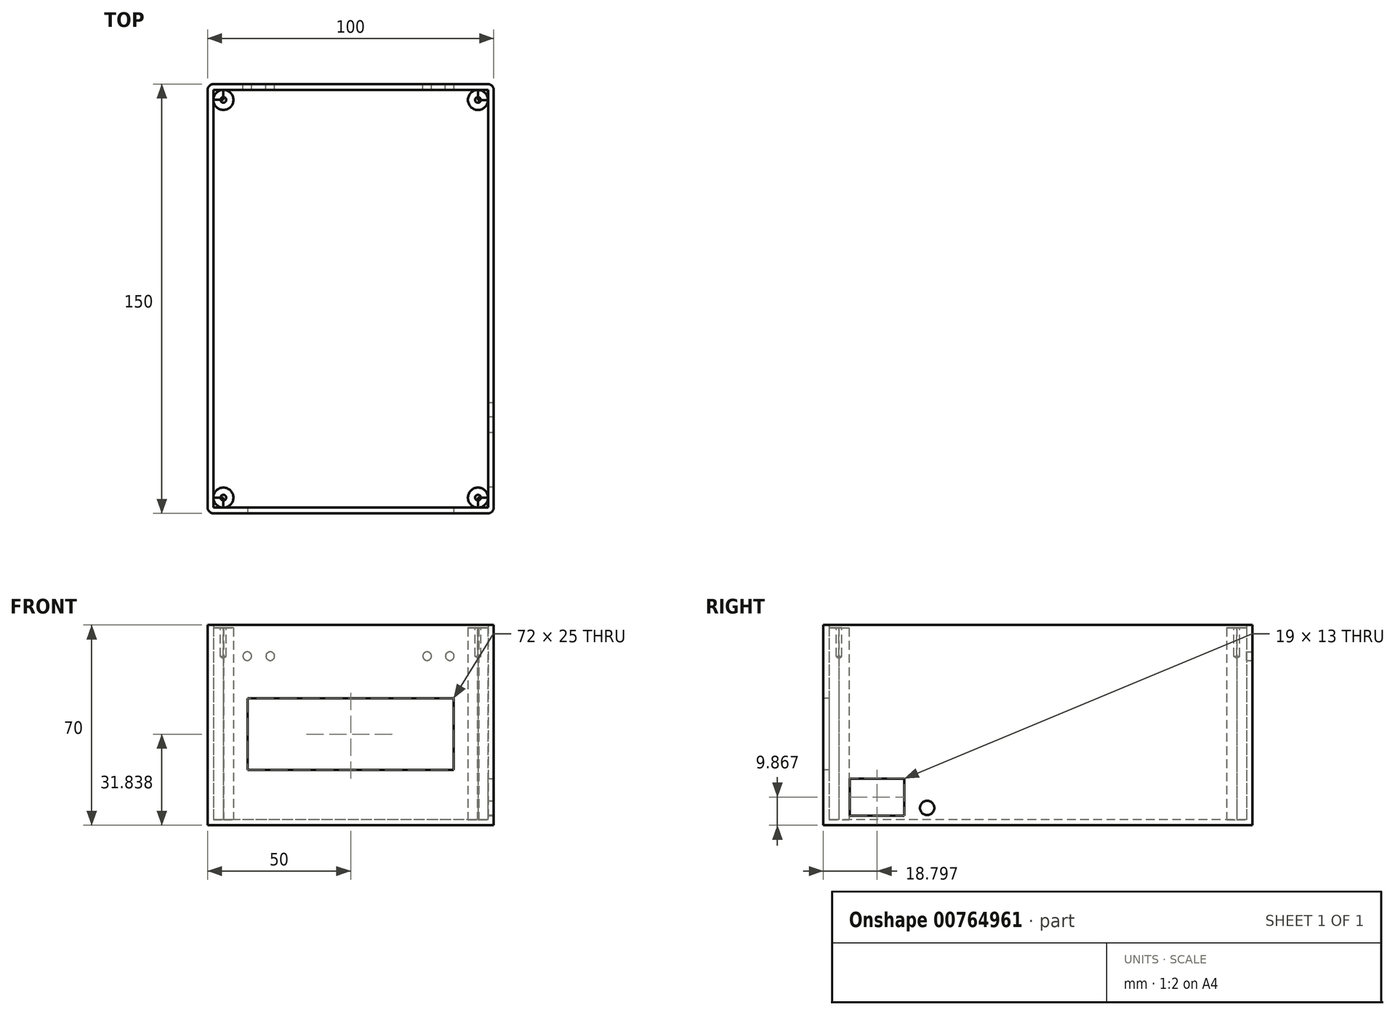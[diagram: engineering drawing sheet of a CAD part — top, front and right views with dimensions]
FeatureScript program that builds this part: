
annotation { "Feature Type Name" : "Feature", "Feature Type Description" : "" }
export const myFeature = defineFeature(function(context is Context, id is Id, definition is map)
    precondition{}
    {
        {
            var Q0;
            Q0=qCreatedBy(makeId("Top.planeOp"),FACE);
            var sketch = newSketch(context, id + "F0", { "sketchPlane" : qUnion([Q0])});
            skLineSegment(sketch, "E0.bottom", {"start": v(50, 75) * mm, "end": v(-50, 75) * mm});
            skLineSegment(sketch, "E0.top", {"start": v(50, -75) * mm, "end": v(-50, -75) * mm});
            skLineSegment(sketch, "E0.left", {"start": v(50, 75) * mm, "end": v(50, -75) * mm});
            skLineSegment(sketch, "E0.right", {"start": v(-50, 75) * mm, "end": v(-50, -75) * mm});
            skPoint(sketch, "E0.middle", {"position": v(0, 0) * mm});
            skSolve(sketch);
        }
        {
            var Q0;
            Q0=qSketchRegion(id+"F0",true);
            extrude(context, id + "F1", {"entities" : qUnion([Q0]), "depth" : 70 * mm, "offsetDistance" : 25.4 * mm});
        }
        {
            var Q0;
            Q0=makeQuery(id+"F1.opExtrude","CAP_FACE",FACE,{"disambiguationData":[OSD([sQuery(id+"F0.wireOp",EDGE,"E0.bottom"),sQuery(id+"F0.wireOp",EDGE,"E0.top"),sQuery(id+"F0.wireOp",EDGE,"E0.left"),sQuery(id+"F0.wireOp",EDGE,"E0.right")])],"isStart":false});
            shell(context, id + "F2", {"entities" : qUnion([Q0]), "thickness" : 2 * mm});
        }
        {
            var Q0;
            Q0=makeQuery(id+"F1.opExtrude","SWEPT_FACE",FACE,{"disambiguationData":[OSD([sQuery(id+"F0.wireOp",EDGE,"E0.top")])]});
            var sketch = newSketch(context, id + "F3", { "sketchPlane" : qUnion([Q0])});
            skLineSegment(sketch, "E1.bottom", {"start": v(-36, 44.34) * mm, "end": v(36, 44.34) * mm});
            skLineSegment(sketch, "E1.top", {"start": v(-36, 19.34) * mm, "end": v(36, 19.34) * mm});
            skLineSegment(sketch, "E1.left", {"start": v(-36, 44.34) * mm, "end": v(-36, 19.34) * mm});
            skLineSegment(sketch, "E1.right", {"start": v(36, 44.34) * mm, "end": v(36, 19.34) * mm});
            skPoint(sketch, "E1.middle", {"position": v(0, 31.84) * mm});
            skSolve(sketch);
        }
        {
            var Q0;
            Q0 = qSketchRegion(id + "F3", true);
            extrude(context, id + "F4", {"entities" : qUnion([Q0]), "operationType" : NewBodyOperationType.REMOVE, "oppositeDirection" : true, "depth" : 3 * mm, "offsetDistance" : 25.4 * mm});
        }
        {
            var Q0;
            Q0=makeQuery(id+"F1.opExtrude","SWEPT_FACE",FACE,{"disambiguationData":[OSD([sQuery(id+"F0.wireOp",EDGE,"E0.bottom")])]});
            var sketch = newSketch(context, id + "F5", { "sketchPlane" : qUnion([Q0])});
            skPoint(sketch, "E2", {"position": v(-34.63, 59.1) * mm});
            skPoint(sketch, "E3", {"position": v(-26.71, 59.1) * mm});
            skPoint(sketch, "E4", {"position": v(36.15, 59.1) * mm});
            skPoint(sketch, "E5", {"position": v(28.12, 59.1) * mm});
            skSolve(sketch);
        }
        {
            var Q0;
            Q0=sQuery(id+"F5.wireOp",VERTEX,"E2");
            var Q1;
            Q1=sQuery(id+"F5.wireOp",VERTEX,"E3");
            var Q2;
            Q2=sQuery(id+"F5.wireOp",VERTEX,"E5");
            var Q3;
            Q3=sQuery(id+"F5.wireOp",VERTEX,"E4");
            var Q4;
            Q4=makeQuery(id+"F1.opExtrude","SWEPT_BODY",BODY,{"disambiguationData":[OSD([sQuery(id+"F0.wireOp",EDGE,"E0.bottom"),sQuery(id+"F0.wireOp",EDGE,"E0.top"),sQuery(id+"F0.wireOp",EDGE,"E0.left"),sQuery(id+"F0.wireOp",EDGE,"E0.right")])]});
            hole(context, id + "F6", {"style" : HoleStyle.SIMPLE, "endStyle" : HoleEndStyle.BLIND, "holeDiameter" : 3 * mm, "majorDiameter" : 6.35 * mm, "holeDepth" : 4 * mm, "isTappedThrough" : true, "tappedDepth" : 12.7 * mm, "tapClearance" : 3, "startFromSketch" : true, "locations" : qUnion([Q0, Q1, Q2, Q3]), "scope" : qUnion([Q4])});
        }
        {
            var Q0;
            Q0=makeQuery(id+"F1.opExtrude","SWEPT_FACE",FACE,{"disambiguationData":[OSD([sQuery(id+"F0.wireOp",EDGE,"E0.left")])]});
            var sketch = newSketch(context, id + "F7", { "sketchPlane" : qUnion([Q0])});
            skPoint(sketch, "E6", {"position": v(-38.7, 6.06) * mm});
            skSolve(sketch);
        }
        {
            var Q0;
            Q0=sQuery(id+"F7.wireOp",VERTEX,"E6");
            var Q1;
            Q1=makeQuery(id+"F1.opExtrude","SWEPT_BODY",BODY,{"disambiguationData":[OSD([sQuery(id+"F0.wireOp",EDGE,"E0.bottom"),sQuery(id+"F0.wireOp",EDGE,"E0.top"),sQuery(id+"F0.wireOp",EDGE,"E0.left"),sQuery(id+"F0.wireOp",EDGE,"E0.right")])]});
            hole(context, id + "F8", {"style" : HoleStyle.SIMPLE, "endStyle" : HoleEndStyle.BLIND, "holeDiameter" : 5 * mm, "majorDiameter" : 6.35 * mm, "holeDepth" : 4 * mm, "isTappedThrough" : true, "tappedDepth" : 12.7 * mm, "tapClearance" : 3, "startFromSketch" : true, "locations" : qUnion([Q0]), "scope" : qUnion([Q1])});
        }
        {
            var Q0;
            Q0=makeQuery(id+"F1.opExtrude","SWEPT_EDGE",EDGE,{"disambiguationData":[OSD([sQuery(id+"F0.wireOp",EDGE,"E0.top"),sQuery(id+"F0.wireOp",EDGE,"E0.right")])]});
            var Q1;
            Q1=makeQuery(id+"F1.opExtrude","SWEPT_EDGE",EDGE,{"disambiguationData":[OSD([sQuery(id+"F0.wireOp",EDGE,"E0.bottom"),sQuery(id+"F0.wireOp",EDGE,"E0.right")])]});
            var Q2;
            Q2=makeQuery(id+"F1.opExtrude","SWEPT_EDGE",EDGE,{"disambiguationData":[OSD([sQuery(id+"F0.wireOp",EDGE,"E0.bottom"),sQuery(id+"F0.wireOp",EDGE,"E0.left")])]});
            var Q3;
            Q3=makeQuery(id+"F1.opExtrude","SWEPT_EDGE",EDGE,{"disambiguationData":[OSD([sQuery(id+"F0.wireOp",EDGE,"E0.top"),sQuery(id+"F0.wireOp",EDGE,"E0.left")])]});
            fillet(context, id + "F9", {"entities" : qUnion([Q0, Q1, Q2, Q3]), "radius" : 2 * mm, "tangentPropagation" : true, "allowEdgeOverflow" : false});
        }
        {
            var Q0;
            Q0=makeQuery(id+"F2.opShell","OFFSET_FACE",FACE,{"disambiguationData":[OSD([sQuery(id+"F0.wireOp",EDGE,"E0.bottom"),sQuery(id+"F0.wireOp",EDGE,"E0.top"),sQuery(id+"F0.wireOp",EDGE,"E0.left"),sQuery(id+"F0.wireOp",EDGE,"E0.right")])]});
            var sketch = newSketch(context, id + "F10", { "sketchPlane" : qUnion([Q0])});
            skCircle(sketch, "E7", {"center": v(-44.5, 69.5) * mm, "radius": 3.5 * mm});
            skSolve(sketch);
        }
        {
            var Q0;
            Q0=makeQuery(id+"F10.imprint","IMPRINT",FACE,{"disambiguationData":[TD([[makeQuery(id+"F10.imprint","IMPRINT",EDGE,{"derivedFrom":sQuery(id+"F10.wireOp",EDGE,"E7")}),-1.0]])]});
            var sketch = newSketch(context, id + "F11", { "sketchPlane" : qUnion([Q0])});
            skCircle(sketch, "E8", {"center": v(44.49, 69.47) * mm, "radius": 3.5 * mm});
            skSolve(sketch);
        }
        {
            var Q0;
            Q0=makeQuery(id+"F10.imprint","IMPRINT",FACE,{"disambiguationData":[TD([[makeQuery(id+"F10.imprint","IMPRINT",EDGE,{"derivedFrom":sQuery(id+"F10.wireOp",EDGE,"E7")}),-1.0]])]});
            var sketch = newSketch(context, id + "F12", { "sketchPlane" : qUnion([Q0])});
            skCircle(sketch, "E9", {"center": v(44.5, -69.5) * mm, "radius": 3.5 * mm});
            skSolve(sketch);
        }
        {
            var Q0;
            Q0=makeQuery(id+"F10.imprint","IMPRINT",FACE,{"disambiguationData":[TD([[makeQuery(id+"F10.imprint","IMPRINT",EDGE,{"derivedFrom":sQuery(id+"F10.wireOp",EDGE,"E7")}),-1.0]])]});
            var sketch = newSketch(context, id + "F13", { "sketchPlane" : qUnion([Q0])});
            skCircle(sketch, "E10", {"center": v(-44.5, -69.5) * mm, "radius": 3.5 * mm});
            skSolve(sketch);
        }
        {
            var Q0;
            Q0 = qSketchRegion(id + "F10", true);
            var Q1;
            Q1 = qSketchRegion(id + "F11", true);
            var Q2;
            Q2 = qSketchRegion(id + "F13", true);
            var Q3;
            Q3 = qSketchRegion(id + "F12", true);
            extrude(context, id + "F14", {"entities" : qUnion([Q0, Q1, Q2, Q3]), "operationType" : NewBodyOperationType.ADD, "depth" : 67 * mm, "offsetDistance" : 25.4 * mm});
        }
        {
            var Q0;
            Q0=makeQuery(id+"F2.opShell","OFFSET_FACE",FACE,{"disambiguationData":[OSD([sQuery(id+"F0.wireOp",EDGE,"E0.bottom"),sQuery(id+"F0.wireOp",EDGE,"E0.top"),sQuery(id+"F0.wireOp",EDGE,"E0.left"),sQuery(id+"F0.wireOp",EDGE,"E0.right")])]});
            var sketch = newSketch(context, id + "F15", { "sketchPlane" : qUnion([Q0])});
            skLineSegment(sketch, "E11.bottom", {"start": v(-44.5, 69.5) * mm, "end": v(-48, 69.5) * mm});
            skLineSegment(sketch, "E11.top", {"start": v(-44.5, 73) * mm, "end": v(-48, 73) * mm});
            skLineSegment(sketch, "E11.left", {"start": v(-44.5, 69.5) * mm, "end": v(-44.5, 73) * mm});
            skLineSegment(sketch, "E11.right", {"start": v(-48, 69.5) * mm, "end": v(-48, 73) * mm});
            skLineSegment(sketch, "E12.bottom", {"start": v(44.49, 69.47) * mm, "end": v(47.99, 69.47) * mm});
            skLineSegment(sketch, "E12.top", {"start": v(44.49, 72.97) * mm, "end": v(47.99, 72.97) * mm});
            skLineSegment(sketch, "E12.left", {"start": v(44.49, 69.47) * mm, "end": v(44.49, 72.97) * mm});
            skLineSegment(sketch, "E12.right", {"start": v(47.99, 69.47) * mm, "end": v(47.99, 72.97) * mm});
            skLineSegment(sketch, "E13.bottom", {"start": v(44.5, -69.5) * mm, "end": v(48, -69.5) * mm});
            skLineSegment(sketch, "E13.top", {"start": v(44.5, -73) * mm, "end": v(48, -73) * mm});
            skLineSegment(sketch, "E13.left", {"start": v(44.5, -69.5) * mm, "end": v(44.5, -73) * mm});
            skLineSegment(sketch, "E13.right", {"start": v(48, -69.5) * mm, "end": v(48, -73) * mm});
            skLineSegment(sketch, "E14.bottom", {"start": v(-44.5, -69.5) * mm, "end": v(-48, -69.5) * mm});
            skLineSegment(sketch, "E14.top", {"start": v(-44.5, -73) * mm, "end": v(-48, -73) * mm});
            skLineSegment(sketch, "E14.left", {"start": v(-44.5, -69.5) * mm, "end": v(-44.5, -73) * mm});
            skLineSegment(sketch, "E14.right", {"start": v(-48, -69.5) * mm, "end": v(-48, -73) * mm});
            skSolve(sketch);
        }
        {
            var Q0;
            Q0 = qSketchRegion(id + "F15", true);
            extrude(context, id + "F16", {"entities" : qUnion([Q0]), "depth" : 67 * mm, "offsetDistance" : 25.4 * mm});
        }
        {
            var Q0;
            Q0=makeQuery(id+"F14.opExtrude","CAP_FACE",FACE,{"disambiguationData":[OSD([sQuery(id+"F10.wireOp",EDGE,"E7")])],"isStart":false});
            var sketch = newSketch(context, id + "F17", { "sketchPlane" : qUnion([Q0])});
            skPoint(sketch, "E15", {"position": v(-44.5, -69.5) * mm});
            skSolve(sketch);
        }
        {
            var Q0;
            Q0=makeQuery(id+"F16.opExtrude","CAP_FACE",FACE,{"disambiguationData":[OSD([sQuery(id+"F15.wireOp",EDGE,"E11.bottom"),sQuery(id+"F15.wireOp",EDGE,"E11.top"),sQuery(id+"F15.wireOp",EDGE,"E11.left"),sQuery(id+"F15.wireOp",EDGE,"E11.right")])],"isStart":false});
            var sketch = newSketch(context, id + "F18", { "sketchPlane" : qUnion([Q0])});
            skPoint(sketch, "E16", {"position": v(-44.5, 69.5) * mm});
            skSolve(sketch);
        }
        {
            var Q0;
            Q0=makeQuery(id+"F16.opExtrude","CAP_FACE",FACE,{"disambiguationData":[OSD([sQuery(id+"F15.wireOp",EDGE,"E12.bottom"),sQuery(id+"F15.wireOp",EDGE,"E12.top"),sQuery(id+"F15.wireOp",EDGE,"E12.left"),sQuery(id+"F15.wireOp",EDGE,"E12.right")])],"isStart":false});
            var sketch = newSketch(context, id + "F19", { "sketchPlane" : qUnion([Q0])});
            skPoint(sketch, "E17", {"position": v(44.49, 69.47) * mm});
            skSolve(sketch);
        }
        {
            var Q0;
            Q0=makeQuery(id+"F16.opExtrude","CAP_FACE",FACE,{"disambiguationData":[OSD([sQuery(id+"F15.wireOp",EDGE,"E13.bottom"),sQuery(id+"F15.wireOp",EDGE,"E13.top"),sQuery(id+"F15.wireOp",EDGE,"E13.left"),sQuery(id+"F15.wireOp",EDGE,"E13.right")])],"isStart":false});
            var sketch = newSketch(context, id + "F20", { "sketchPlane" : qUnion([Q0])});
            skPoint(sketch, "E18", {"position": v(44.5, -69.5) * mm});
            skSolve(sketch);
        }
        {
            var Q0;
            Q0=sQuery(id+"F17.wireOp",VERTEX,"E15");
            var Q1;
            Q1=sQuery(id+"F18.wireOp",VERTEX,"E16");
            var Q2;
            Q2=sQuery(id+"F19.wireOp",VERTEX,"E17");
            var Q3;
            Q3=sQuery(id+"F20.wireOp",VERTEX,"E18");
            var Q4;
            Q4=makeQuery(id+"F1.opExtrude","SWEPT_BODY",BODY,{"disambiguationData":[OSD([sQuery(id+"F0.wireOp",EDGE,"E0.bottom"),sQuery(id+"F0.wireOp",EDGE,"E0.top"),sQuery(id+"F0.wireOp",EDGE,"E0.left"),sQuery(id+"F0.wireOp",EDGE,"E0.right")])]});
            var Q5;
            Q5=makeQuery(id+"F16.opExtrude","SWEPT_BODY",BODY,{"disambiguationData":[OSD([sQuery(id+"F15.wireOp",EDGE,"E14.bottom"),sQuery(id+"F15.wireOp",EDGE,"E14.top"),sQuery(id+"F15.wireOp",EDGE,"E14.left"),sQuery(id+"F15.wireOp",EDGE,"E14.right")])]});
            var Q6;
            Q6=makeQuery(id+"F16.opExtrude","SWEPT_BODY",BODY,{"disambiguationData":[OSD([sQuery(id+"F15.wireOp",EDGE,"E11.bottom"),sQuery(id+"F15.wireOp",EDGE,"E11.top"),sQuery(id+"F15.wireOp",EDGE,"E11.left"),sQuery(id+"F15.wireOp",EDGE,"E11.right")])]});
            var Q7;
            Q7=makeQuery(id+"F16.opExtrude","SWEPT_BODY",BODY,{"disambiguationData":[OSD([sQuery(id+"F15.wireOp",EDGE,"E12.bottom"),sQuery(id+"F15.wireOp",EDGE,"E12.top"),sQuery(id+"F15.wireOp",EDGE,"E12.left"),sQuery(id+"F15.wireOp",EDGE,"E12.right")])]});
            var Q8;
            Q8=makeQuery(id+"F16.opExtrude","SWEPT_BODY",BODY,{"disambiguationData":[OSD([sQuery(id+"F15.wireOp",EDGE,"E13.bottom"),sQuery(id+"F15.wireOp",EDGE,"E13.top"),sQuery(id+"F15.wireOp",EDGE,"E13.left"),sQuery(id+"F15.wireOp",EDGE,"E13.right")])]});
            hole(context, id + "F21", {"style" : HoleStyle.SIMPLE, "endStyle" : HoleEndStyle.BLIND, "holeDiameter" : 2 * mm, "majorDiameter" : 6.35 * mm, "holeDepth" : 10 * mm, "isTappedThrough" : true, "tappedDepth" : 12.7 * mm, "tapClearance" : 3, "startFromSketch" : true, "locations" : qUnion([Q0, Q1, Q2, Q3]), "scope" : qUnion([Q4, Q5, Q6, Q7, Q8])});
        }
        {
            var Q0;
            Q0=makeQuery(id+"F1.opExtrude","SWEPT_FACE",FACE,{"disambiguationData":[OSD([sQuery(id+"F0.wireOp",EDGE,"E0.left")])]});
            var sketch = newSketch(context, id + "F22", { "sketchPlane" : qUnion([Q0])});
            skLineSegment(sketch, "E19.bottom", {"start": v(-65.7, 3.37) * mm, "end": v(-46.7, 3.37) * mm});
            skLineSegment(sketch, "E19.top", {"start": v(-65.7, 16.37) * mm, "end": v(-46.7, 16.37) * mm});
            skLineSegment(sketch, "E19.left", {"start": v(-65.7, 3.37) * mm, "end": v(-65.7, 16.37) * mm});
            skLineSegment(sketch, "E19.right", {"start": v(-46.7, 3.37) * mm, "end": v(-46.7, 16.37) * mm});
            skPoint(sketch, "E19.middle", {"position": v(-54.68, 16.22) * mm});
            skSolve(sketch);
        }
        {
            var Q0;
            Q0 = qSketchRegion(id + "F22", true);
            extrude(context, id + "F23", {"entities" : qUnion([Q0]), "operationType" : NewBodyOperationType.REMOVE, "oppositeDirection" : true, "depth" : 25.4 * mm, "offsetDistance" : 25.4 * mm});
        }
    });
